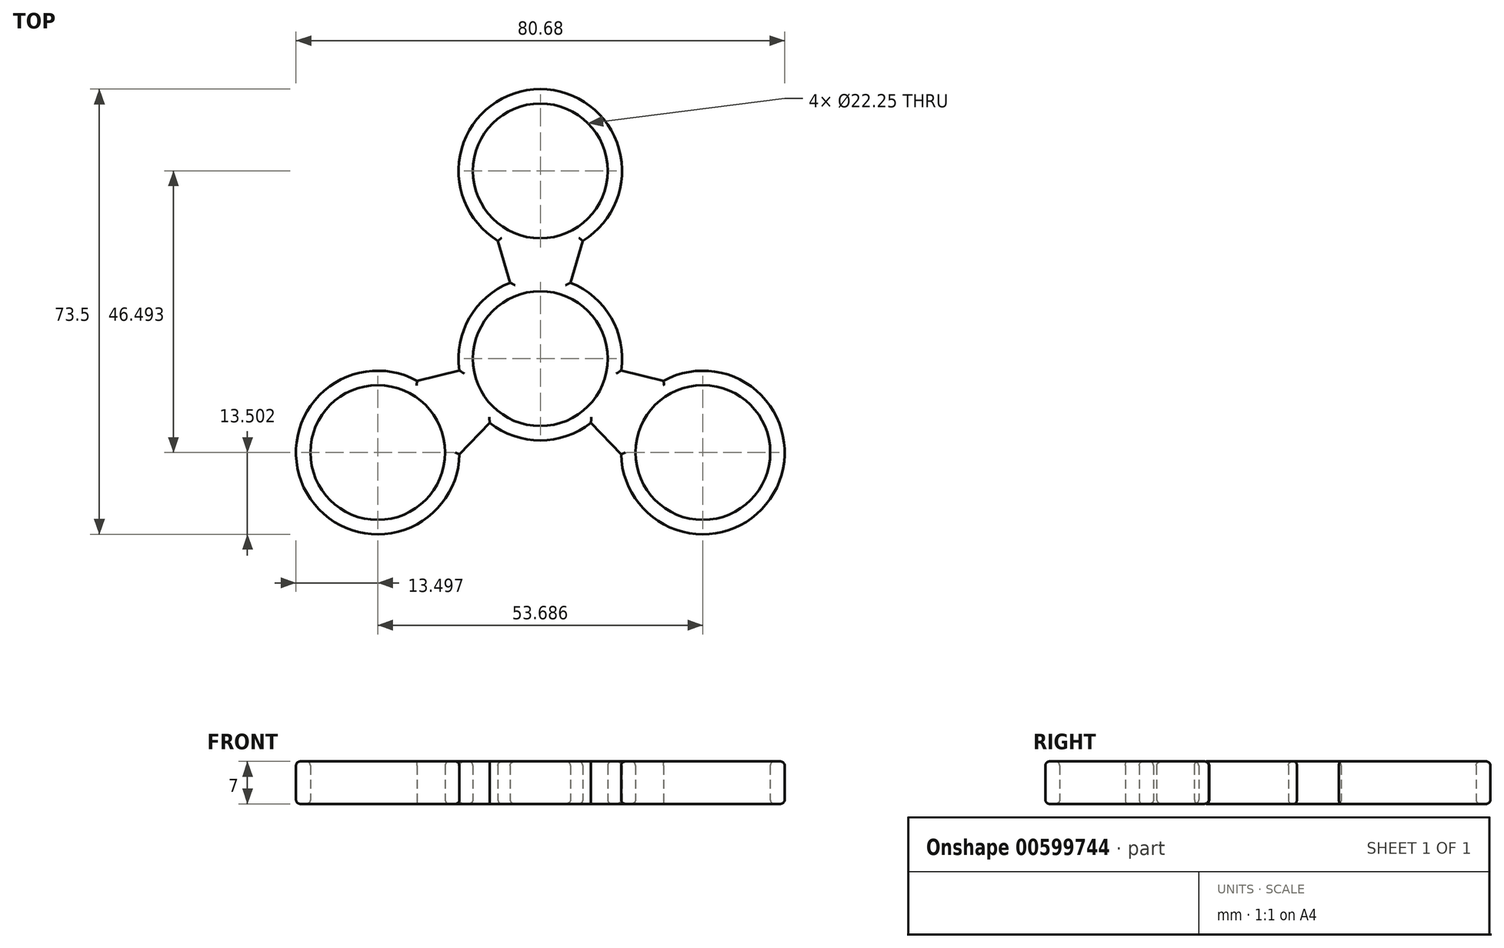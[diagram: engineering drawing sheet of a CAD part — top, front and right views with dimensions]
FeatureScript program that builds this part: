
annotation { "Feature Type Name" : "Feature", "Feature Type Description" : "" }
export const myFeature = defineFeature(function(context is Context, id is Id, definition is map)
    precondition{}
    {
        {
            var Q0;
            Q0=qCreatedBy(makeId("Top.planeOp"),FACE);
            var sketch = newSketch(context, id + "F0", { "sketchPlane" : qUnion([Q0])});
            skCircle(sketch, "E0", {"center": v(0, 0) * mm, "radius": 11.12 * mm});
            skCircle(sketch, "E1", {"center": v(0, 0) * mm, "radius": 13.5 * mm});
            skCircle(sketch, "E2", {"center": v(0, 31) * mm, "radius": 11.12 * mm});
            skCircle(sketch, "E3", {"center": v(0, 31) * mm, "radius": 13.5 * mm});
            skPoint(sketch, "E4", {"position": v(0, 13.5) * mm});
            skPoint(sketch, "E5", {"position": v(5, 12.54) * mm});
            skPoint(sketch, "E6", {"position": v(-5, 12.54) * mm});
            skPoint(sketch, "E7", {"position": v(0, 17.5) * mm});
            skPoint(sketch, "E8", {"position": v(7, 19.45) * mm});
            skPoint(sketch, "E9", {"position": v(-7, 19.45) * mm});
            skLineSegment(sketch, "E10", {"start": v(-5, 12.54) * mm, "end": v(-7, 19.45) * mm});
            skLineSegment(sketch, "E11", {"start": v(5, 12.54) * mm, "end": v(7, 19.45) * mm});
            skCircle(sketch, "E12.1.0", {"center": v(-26.84, -15.5) * mm, "radius": 13.5 * mm});
            skCircle(sketch, "E12.1.1", {"center": v(-26.84, -15.5) * mm, "radius": 11.12 * mm});
            skLineSegment(sketch, "E12.1.2", {"start": v(-8.36, -10.6) * mm, "end": v(-13.35, -15.79) * mm});
            skLineSegment(sketch, "E12.1.3", {"start": v(-13.36, -1.94) * mm, "end": v(-20.35, -3.66) * mm});
            skCircle(sketch, "E12.2.0", {"center": v(26.84, -15.5) * mm, "radius": 13.5 * mm});
            skCircle(sketch, "E12.2.1", {"center": v(26.84, -15.5) * mm, "radius": 11.12 * mm});
            skLineSegment(sketch, "E12.2.2", {"start": v(13.36, -1.94) * mm, "end": v(20.35, -3.66) * mm});
            skLineSegment(sketch, "E12.2.3", {"start": v(8.36, -10.6) * mm, "end": v(13.35, -15.79) * mm});
            skSolve(sketch);
        }
        {
            var Q0;
            Q0 = qSketchRegion(id + "F0", true);
            extrude(context, id + "F1", {"entities" : qUnion([Q0]), "depth" : 7 * mm, "offsetDistance" : 25 * mm});
        }
        {
            var Q0;
            Q0=makeQuery(id+"F1.opExtrude","CAP_FACE",FACE,{"disambiguationData":[OSD([sQuery(id+"F0.wireOp",EDGE,"E0"),sQuery(id+"F0.wireOp",EDGE,"E1"),sQuery(id+"F0.wireOp",EDGE,"E2"),sQuery(id+"F0.wireOp",EDGE,"E3"),sQuery(id+"F0.wireOp",EDGE,"E10"),sQuery(id+"F0.wireOp",EDGE,"E11"),sQuery(id+"F0.wireOp",EDGE,"E12.1.0"),sQuery(id+"F0.wireOp",EDGE,"E12.1.1"),sQuery(id+"F0.wireOp",EDGE,"E12.1.2"),sQuery(id+"F0.wireOp",EDGE,"E12.1.3"),sQuery(id+"F0.wireOp",EDGE,"E12.2.0"),sQuery(id+"F0.wireOp",EDGE,"E12.2.1"),sQuery(id+"F0.wireOp",EDGE,"E12.2.2"),sQuery(id+"F0.wireOp",EDGE,"E12.2.3")])],"isStart":false});
            var Q1;
            Q1=makeQuery(id+"F1.opExtrude","CAP_FACE",FACE,{"disambiguationData":[OSD([sQuery(id+"F0.wireOp",EDGE,"E0"),sQuery(id+"F0.wireOp",EDGE,"E1"),sQuery(id+"F0.wireOp",EDGE,"E2"),sQuery(id+"F0.wireOp",EDGE,"E3"),sQuery(id+"F0.wireOp",EDGE,"E10"),sQuery(id+"F0.wireOp",EDGE,"E11"),sQuery(id+"F0.wireOp",EDGE,"E12.1.0"),sQuery(id+"F0.wireOp",EDGE,"E12.1.1"),sQuery(id+"F0.wireOp",EDGE,"E12.1.2"),sQuery(id+"F0.wireOp",EDGE,"E12.1.3"),sQuery(id+"F0.wireOp",EDGE,"E12.2.0"),sQuery(id+"F0.wireOp",EDGE,"E12.2.1"),sQuery(id+"F0.wireOp",EDGE,"E12.2.2"),sQuery(id+"F0.wireOp",EDGE,"E12.2.3")])],"isStart":true});
            fillet(context, id + "F2", {"entities" : qUnion([Q0, Q1]), "radius" : .7 * mm, "tangentPropagation" : true, "allowEdgeOverflow" : false});
        }
    });
